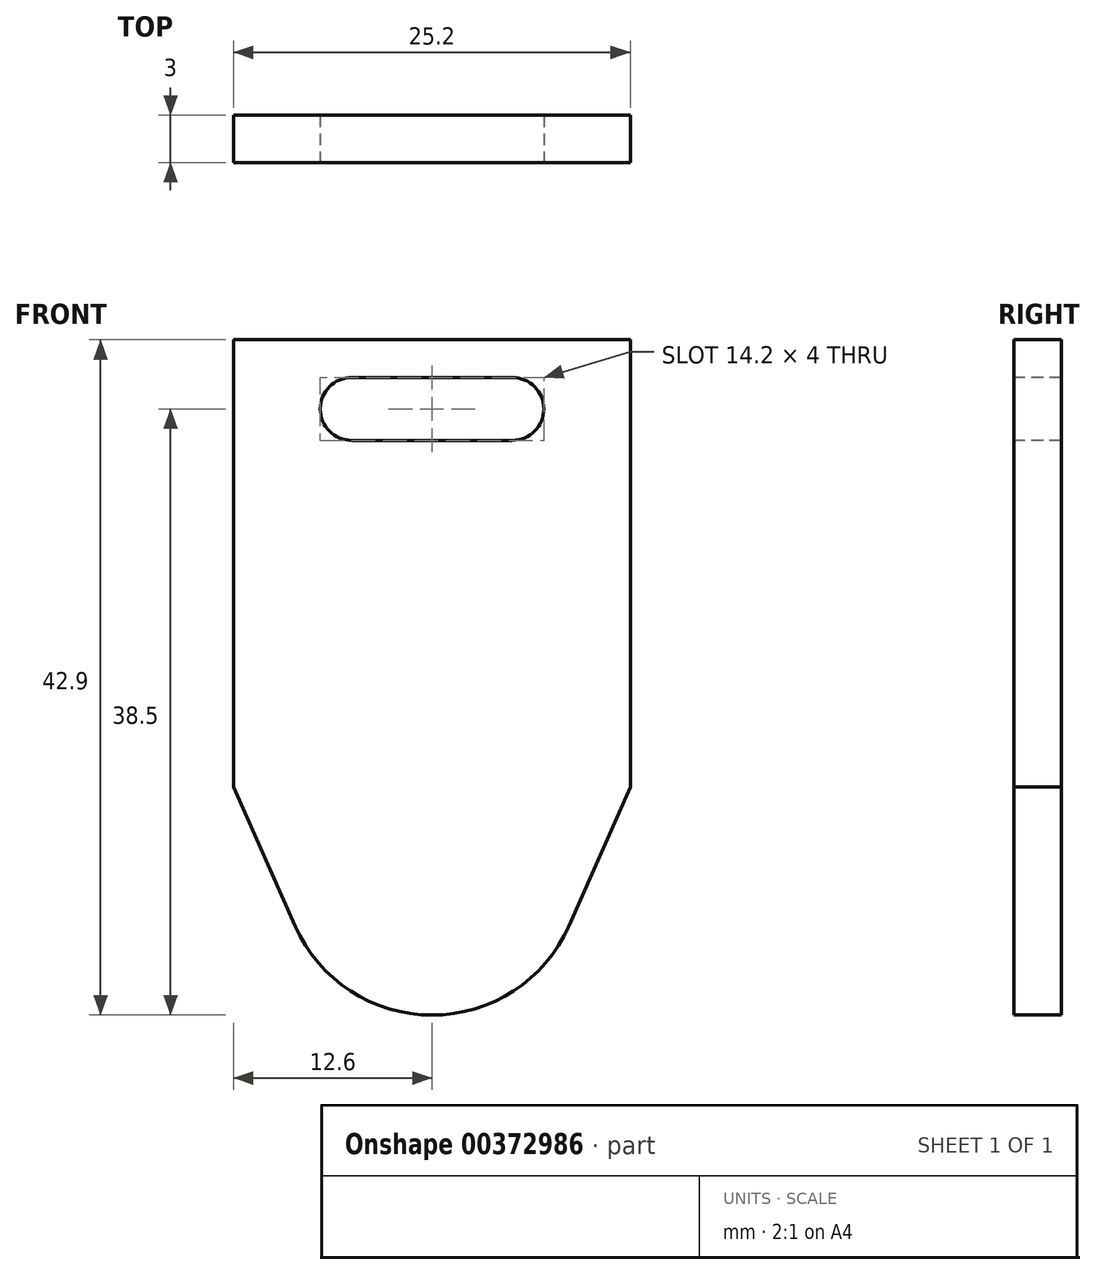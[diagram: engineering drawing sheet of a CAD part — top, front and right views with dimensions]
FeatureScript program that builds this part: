
annotation { "Feature Type Name" : "Feature", "Feature Type Description" : "" }
export const myFeature = defineFeature(function(context is Context, id is Id, definition is map)
    precondition{}
    {
        {
            var Q0;
            Q0=qCreatedBy(makeId("Front.planeOp"),FACE);
            var sketch = newSketch(context, id + "F0", { "sketchPlane" : qUnion([Q0])});
            skLineSegment(sketch, "E0", {"start": v(-12.6, 5) * mm, "end": v(-12.6, 33.4) * mm});
            skLineSegment(sketch, "E1", {"start": v(-12.6, 33.4) * mm, "end": v(12.6, 33.4) * mm});
            skLineSegment(sketch, "E2", {"start": v(12.6, 33.4) * mm, "end": v(12.6, 5) * mm});
            skArc(sketch, "E3", {"start": v(-8.69, -3.84) * mm, "mid": v(0, -9.5) * mm, "end": v(8.69, -3.84) * mm});
            skLineSegment(sketch, "E4", {"start": v(-8.69, -3.84) * mm, "end": v(-12.6, 5) * mm});
            skLineSegment(sketch, "E5", {"start": v(0, 0) * mm, "end": v(0, 19.5) * mm, "construction": true});
            skLineSegment(sketch, "E6.MirrorCS", {"start": v(8.69, -3.84) * mm, "end": v(12.6, 5) * mm});
            skPoint(sketch, "E7.orphan", {"position": v(-12.6, 0) * mm});
            skSolve(sketch);
        }
        {
            var Q0;
            Q0 = qSketchRegion(id + "F0", true);
            extrude(context, id + "F1", {"entities" : qUnion([Q0]), "offsetDistance" : 25 * mm, "depth" : 3 * mm});
        }
        {
            var Q0;
            Q0=makeQuery(id+"F1.opExtrude","CAP_FACE",FACE,{"disambiguationData":[OSD([sQuery(id+"F0.wireOp",EDGE,"aGBM36Wp-XQA9-ZKUJ-xuBQ-YqOXaFc0oGf6"),sQuery(id+"F0.wireOp",EDGE,"E0"),sQuery(id+"F0.wireOp",EDGE,"E1"),sQuery(id+"F0.wireOp",EDGE,"E2")])],"isStart":false});
            var sketch = newSketch(context, id + "F2", { "sketchPlane" : qUnion([Q0])});
            skArc(sketch, "E8", {"start": v(-5.1, 31) * mm, "mid": v(-7.1, 29) * mm, "end": v(-5.1, 27) * mm});
            skLineSegment(sketch, "E9", {"start": v(0, 0) * mm, "end": v(0, 26.92) * mm, "construction": true});
            skLineSegment(sketch, "E10", {"start": v(-5.1, 31) * mm, "end": v(0, 31) * mm});
            skLineSegment(sketch, "E11", {"start": v(-5.1, 27) * mm, "end": v(0, 27) * mm});
            skArc(sketch, "E12.MirrorCS", {"start": v(5.1, 31) * mm, "mid": v(7.1, 29) * mm, "end": v(5.1, 27) * mm});
            skLineSegment(sketch, "E13.MirrorCS", {"start": v(5.1, 31) * mm, "end": v(0, 31) * mm});
            skLineSegment(sketch, "E14.MirrorCS", {"start": v(5.1, 27) * mm, "end": v(0, 27) * mm});
            skSolve(sketch);
        }
        {
            var Q0;
            Q0 = qSketchRegion(id + "F2", true);
            extrude(context, id + "F3", {"entities" : qUnion([Q0]), "operationType" : NewBodyOperationType.REMOVE, "oppositeDirection" : true, "depth" : 25 * mm, "offsetDistance" : 25 * mm});
        }
    });
